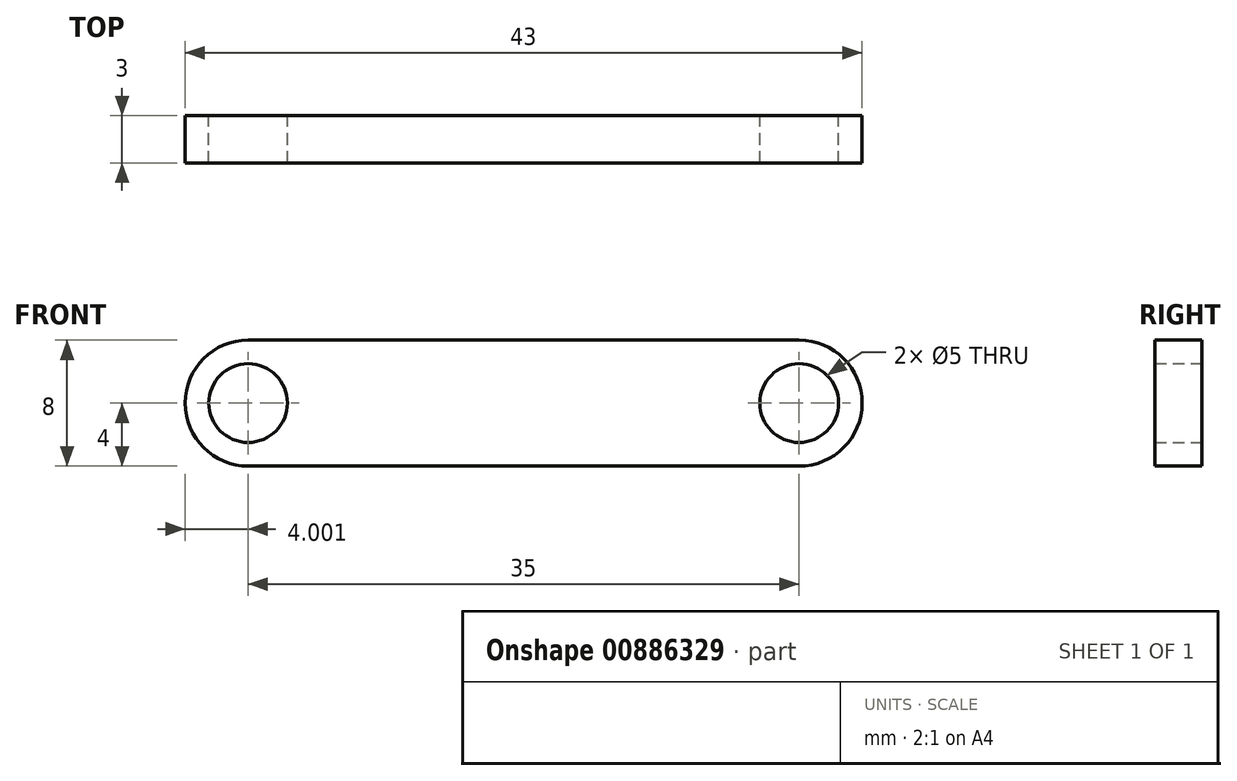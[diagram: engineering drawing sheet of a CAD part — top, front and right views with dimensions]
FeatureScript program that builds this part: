
annotation { "Feature Type Name" : "Feature", "Feature Type Description" : "" }
export const myFeature = defineFeature(function(context is Context, id is Id, definition is map)
    precondition{}
    {
        {
            var Q0;
            Q0=qCreatedBy(makeId("Front.planeOp"),FACE);
            var sketch = newSketch(context, id + "F0", { "sketchPlane" : qUnion([Q0])});
            skLineSegment(sketch, "E0.bottom", {"start": v(-15.85, 24.62) * mm, "end": v(19.15, 24.62) * mm});
            skLineSegment(sketch, "E0.top", {"start": v(-15.85, 16.62) * mm, "end": v(19.15, 16.62) * mm});
            skArc(sketch, "E1", {"start": v(-15.85, 24.62) * mm, "mid": v(-19.85, 20.62) * mm, "end": v(-15.85, 16.62) * mm});
            skArc(sketch, "E2", {"start": v(19.15, 16.62) * mm, "mid": v(23.15, 20.62) * mm, "end": v(19.15, 24.62) * mm});
            skCircle(sketch, "E3", {"center": v(-15.85, 20.62) * mm, "radius": 2.5 * mm});
            skCircle(sketch, "E4", {"center": v(19.15, 20.62) * mm, "radius": 2.5 * mm});
            skSolve(sketch);
        }
        {
            var Q0;
            Q0=makeQuery(id+"F0.imprint","IMPRINT",FACE,{"disambiguationData":[TD([[makeQuery(id+"F0.imprint","IMPRINT",EDGE,{"derivedFrom":sQuery(id+"F0.wireOp",EDGE,"E0.bottom")}),-1.0]])]});
            extrude(context, id + "F1", {"entities" : qUnion([Q0]), "depth" : 3 * mm, "offsetDistance" : 25 * mm});
        }
    });
